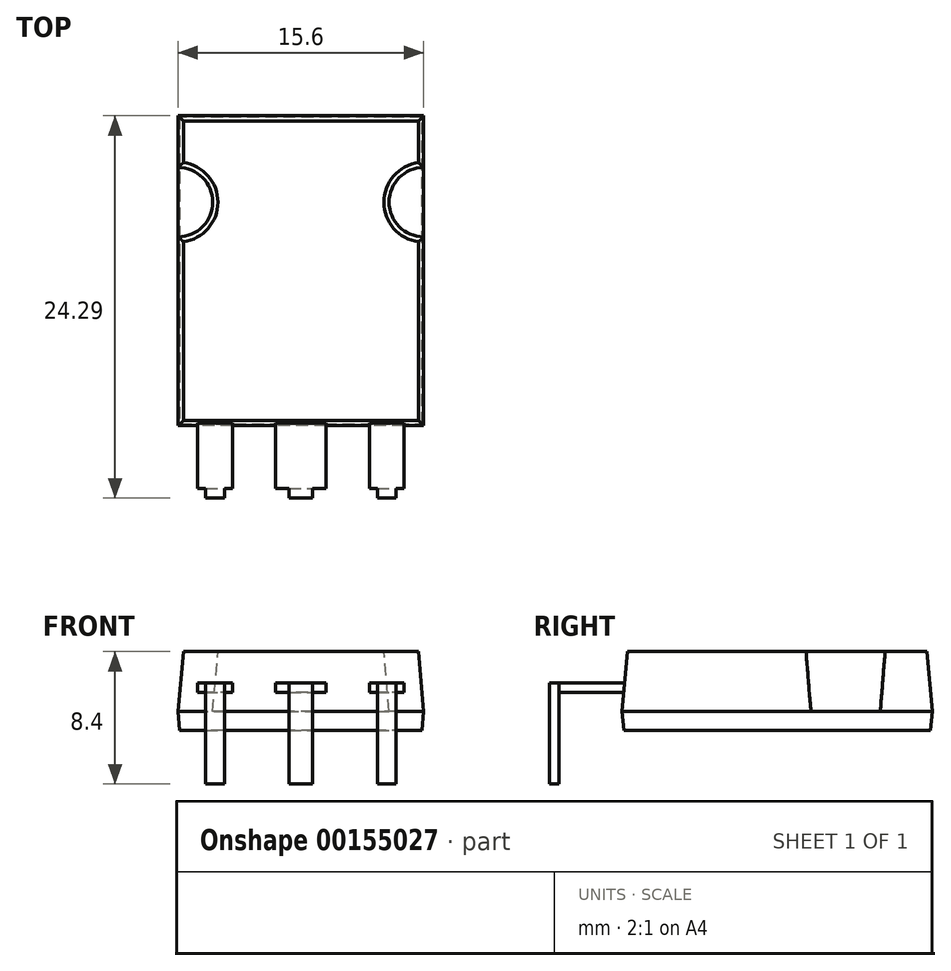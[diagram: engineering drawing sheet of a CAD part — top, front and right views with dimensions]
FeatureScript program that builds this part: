
annotation { "Feature Type Name" : "Feature", "Feature Type Description" : "" }
export const myFeature = defineFeature(function(context is Context, id is Id, definition is map)
    precondition{}
    {
        {
            assignVariable(context, id + "F0", {"name" : "D", "anyValue" : 2.4});
        }
        {
            assignVariable(context, id + "F1", {"name" : "A", "anyValue" : 5});
        }
        {
            var Q0;
            Q0=qCreatedBy(makeId("Top.planeOp"),FACE);
            var sketch = newSketch(context, id + "F2", { "sketchPlane" : qUnion([Q0])});
            skLineSegment(sketch, "E0.bottom", {"start": v(-7.8, 19.7) * mm, "end": v(7.8, 19.7) * mm});
            skLineSegment(sketch, "E0.top", {"start": v(-7.8, 0) * mm, "end": v(7.8, 0) * mm});
            skLineSegment(sketch, "E0.left", {"start": v(-7.8, 19.7) * mm, "end": v(-7.8, 16.4) * mm});
            skLineSegment(sketch, "E0.right", {"start": v(7.8, 19.7) * mm, "end": v(7.8, 16.4) * mm});
            skArc(sketch, "E1", {"start": v(-7.8, 12) * mm, "mid": v(-5.6, 14.2) * mm, "end": v(-7.8, 16.4) * mm});
            skArc(sketch, "E2.MirrorCS", {"start": v(7.8, 12) * mm, "mid": v(5.6, 14.2) * mm, "end": v(7.8, 16.4) * mm});
            skLineSegment(sketch, "E3.trimOffspring", {"start": v(-7.8, 12) * mm, "end": v(-7.8, 0) * mm});
            skLineSegment(sketch, "E4.trimOffspring", {"start": v(7.8, 12) * mm, "end": v(7.8, 0) * mm});
            skSolve(sketch);
        }
        {
            var Q0;
            Q0 = qSketchRegion(id + "F2", true);
            extrude(context, id + "F3", {"entities" : qUnion([Q0]), "depth" : (getVariable(context, 'A') - (getVariable(context, 'D') / 2)) * mm, "hasDraft" : true, "draftAngle" : 5 * degree, "draftPullDirection" : true});
        }
        {
            var Q0;
            Q0=makeQuery(id+"F3.opExtrude","CAP_FACE",FACE,{"disambiguationData":[OSD([sQuery(id+"F2.wireOp",EDGE,"E0.bottom"),sQuery(id+"F2.wireOp",EDGE,"E0.top"),sQuery(id+"F2.wireOp",EDGE,"E0.left"),sQuery(id+"F2.wireOp",EDGE,"E0.right"),sQuery(id+"F2.wireOp",EDGE,"E1"),sQuery(id+"F2.wireOp",EDGE,"E2.MirrorCS"),sQuery(id+"F2.wireOp",EDGE,"E3.trimOffspring"),sQuery(id+"F2.wireOp",EDGE,"E4.trimOffspring")])],"isStart":true});
            var sketch = newSketch(context, id + "F4", { "sketchPlane" : qUnion([Q0])});
            skLineSegment(sketch, "E5.0", {"start": v(-7.8, -19.7) * mm, "end": v(7.8, -19.7) * mm});
            skLineSegment(sketch, "E5.1", {"start": v(-7.8, 0) * mm, "end": v(7.8, 0) * mm});
            skLineSegment(sketch, "E6", {"start": v(-7.8, -19.7) * mm, "end": v(-7.8, 0) * mm});
            skLineSegment(sketch, "E7", {"start": v(7.8, 0) * mm, "end": v(7.8, -19.7) * mm});
            skSolve(sketch);
        }
        {
            var Q0;
            Q0 = qSketchRegion(id + "F4", true);
            extrude(context, id + "F5", {"entities" : qUnion([Q0]), "operationType" : NewBodyOperationType.ADD, "depth" : (getVariable(context, 'D') / 2) * mm, "hasDraft" : true, "draftAngle" : 5 * degree, "draftPullDirection" : true});
        }
        {
            var Q0;
            Q0=qCreatedBy(makeId("Top.planeOp"),FACE);
            cPlane(context, id + "F6", {"entities" : qUnion([Q0]), "cplaneType" : CPlaneType.OFFSET, "offset" : (getVariable(context, 'D') / 2) * mm, "width" : 150 * mm, "height" : 150 * mm});
        }
        {
            var Q0;
            Q0=qCreatedBy(id+"F6.planeOp",FACE);
            var sketch = newSketch(context, id + "F7", { "sketchPlane" : qUnion([Q0])});
            skLineSegment(sketch, "E8.bottom", {"start": v(-1.6, 0) * mm, "end": v(1.6, 0) * mm});
            skLineSegment(sketch, "E8.top", {"start": v(-1.6, -4) * mm, "end": v(1.6, -4) * mm});
            skLineSegment(sketch, "E8.left", {"start": v(-1.6, 0) * mm, "end": v(-1.6, -4) * mm});
            skLineSegment(sketch, "E8.right", {"start": v(1.6, 0) * mm, "end": v(1.6, -4) * mm});
            skLineSegment(sketch, "E9.bottom", {"start": v(-6.55, 0) * mm, "end": v(-4.35, 0) * mm});
            skLineSegment(sketch, "E9.top", {"start": v(-6.55, -4) * mm, "end": v(-4.35, -4) * mm});
            skLineSegment(sketch, "E9.left", {"start": v(-4.35, 0) * mm, "end": v(-4.35, -4) * mm});
            skLineSegment(sketch, "E9.right", {"start": v(-6.55, 0) * mm, "end": v(-6.55, -4) * mm});
            skPoint(sketch, "E10", {"position": v(-5.45, -4) * mm});
            skPoint(sketch, "E11.MirrorP", {"position": v(5.45, -4) * mm});
            skLineSegment(sketch, "E12.MirrorCS", {"start": v(6.55, 0) * mm, "end": v(4.35, 0) * mm});
            skLineSegment(sketch, "E13.MirrorCS", {"start": v(6.55, -4) * mm, "end": v(4.35, -4) * mm});
            skLineSegment(sketch, "E14.MirrorCS", {"start": v(4.35, 0) * mm, "end": v(4.35, -4) * mm});
            skLineSegment(sketch, "E15.MirrorCS", {"start": v(6.55, 0) * mm, "end": v(6.55, -4) * mm});
            skLineSegment(sketch, "E16.top", {"start": v(-6.55, 1) * mm, "end": v(-4.35, 1) * mm});
            skLineSegment(sketch, "E16.left", {"start": v(-6.55, 0) * mm, "end": v(-6.55, 1) * mm});
            skLineSegment(sketch, "E16.right", {"start": v(-4.35, 0) * mm, "end": v(-4.35, 1) * mm});
            skLineSegment(sketch, "E17.top", {"start": v(-1.6, 1) * mm, "end": v(1.6, 1) * mm});
            skLineSegment(sketch, "E17.left", {"start": v(-1.6, 0) * mm, "end": v(-1.6, 1) * mm});
            skLineSegment(sketch, "E17.right", {"start": v(1.6, 0) * mm, "end": v(1.6, 1) * mm});
            skLineSegment(sketch, "E18.bottom", {"start": v(4.35, 0) * mm, "end": v(6.55, 0) * mm});
            skLineSegment(sketch, "E18.top", {"start": v(4.35, 1) * mm, "end": v(6.55, 1) * mm});
            skLineSegment(sketch, "E18.left", {"start": v(4.35, 0) * mm, "end": v(4.35, 1) * mm});
            skLineSegment(sketch, "E18.right", {"start": v(6.55, 0) * mm, "end": v(6.55, 1) * mm});
            skLineSegment(sketch, "E19.bottom", {"start": v(-6.05, -4) * mm, "end": v(-4.85, -4) * mm});
            skLineSegment(sketch, "E19.top", {"start": v(-6.05, -4.6) * mm, "end": v(-4.85, -4.6) * mm});
            skLineSegment(sketch, "E19.left", {"start": v(-6.05, -4) * mm, "end": v(-6.05, -4.6) * mm});
            skLineSegment(sketch, "E19.right", {"start": v(-4.85, -4) * mm, "end": v(-4.85, -4.6) * mm});
            skLineSegment(sketch, "E20.bottom", {"start": v(-0.75, -4) * mm, "end": v(0.75, -4) * mm});
            skLineSegment(sketch, "E20.top", {"start": v(-0.75, -4.6) * mm, "end": v(0.75, -4.6) * mm});
            skLineSegment(sketch, "E20.left", {"start": v(-0.75, -4) * mm, "end": v(-0.75, -4.6) * mm});
            skLineSegment(sketch, "E20.right", {"start": v(0.75, -4) * mm, "end": v(0.75, -4.6) * mm});
            skLineSegment(sketch, "E21.MirrorCS", {"start": v(4.85, -4) * mm, "end": v(4.85, -4.6) * mm});
            skLineSegment(sketch, "E22.MirrorCS", {"start": v(6.05, -4.6) * mm, "end": v(4.85, -4.6) * mm});
            skLineSegment(sketch, "E23.MirrorCS", {"start": v(6.05, -4) * mm, "end": v(4.85, -4) * mm});
            skLineSegment(sketch, "E24.MirrorCS", {"start": v(6.05, -4) * mm, "end": v(6.05, -4.6) * mm});
            skPoint(sketch, "E25", {"position": v(0, -4) * mm});
            skSolve(sketch);
        }
        {
            var Q0;
            Q0 = qSketchRegion(id + "F7", true);
            extrude(context, id + "F8", {"entities" : qUnion([Q0]), "operationType" : NewBodyOperationType.ADD, "depth" : .6 * mm});
        }
        {
            var Q0;
            Q0=makeQuery(id+"F8.opExtrude","CAP_FACE",FACE,{"disambiguationData":[OSD([sQuery(id+"F7.wireOp",EDGE,"E9.top"),sQuery(id+"F7.wireOp",EDGE,"E9.left"),sQuery(id+"F7.wireOp",EDGE,"E9.right"),sQuery(id+"F7.wireOp",EDGE,"E16.top"),sQuery(id+"F7.wireOp",EDGE,"E16.left"),sQuery(id+"F7.wireOp",EDGE,"E16.right"),sQuery(id+"F7.wireOp",EDGE,"E19.top"),sQuery(id+"F7.wireOp",EDGE,"E19.left"),sQuery(id+"F7.wireOp",EDGE,"E19.right")])],"isStart":true});
            var sketch = newSketch(context, id + "F9", { "sketchPlane" : qUnion([Q0])});
            skLineSegment(sketch, "E26.bottom", {"start": v(-6.05, 4.6) * mm, "end": v(-4.85, 4.6) * mm});
            skLineSegment(sketch, "E26.top", {"start": v(-6.05, 4) * mm, "end": v(-4.85, 4) * mm});
            skLineSegment(sketch, "E26.left", {"start": v(-6.05, 4.6) * mm, "end": v(-6.05, 4) * mm});
            skLineSegment(sketch, "E26.right", {"start": v(-4.85, 4.6) * mm, "end": v(-4.85, 4) * mm});
            skPoint(sketch, "E27.2", {"position": v(4.85, 4.6) * mm});
            skPoint(sketch, "E27.3", {"position": v(6.05, 4) * mm});
            skLineSegment(sketch, "E28.bottom", {"start": v(4.85, 4.6) * mm, "end": v(6.05, 4.6) * mm});
            skLineSegment(sketch, "E28.top", {"start": v(4.85, 4) * mm, "end": v(6.05, 4) * mm});
            skLineSegment(sketch, "E28.left", {"start": v(4.85, 4.6) * mm, "end": v(4.85, 4) * mm});
            skLineSegment(sketch, "E28.right", {"start": v(6.05, 4.6) * mm, "end": v(6.05, 4) * mm});
            skLineSegment(sketch, "E29.0", {"start": v(-0.75, 4) * mm, "end": v(-0.75, 4.6) * mm});
            skLineSegment(sketch, "E30.0", {"start": v(-0.75, 4.6) * mm, "end": v(0.75, 4.6) * mm});
            skLineSegment(sketch, "E31.0", {"start": v(0.75, 4) * mm, "end": v(0.75, 4.6) * mm});
            skLineSegment(sketch, "E32", {"start": v(-0.75, 4) * mm, "end": v(0.75, 4) * mm});
            skSolve(sketch);
        }
        {
            var Q0;
            Q0 = qSketchRegion(id + "F9", true);
            extrude(context, id + "F10", {"entities" : qUnion([Q0]), "operationType" : NewBodyOperationType.ADD, "depth" : 5.8 * mm});
        }
    });
